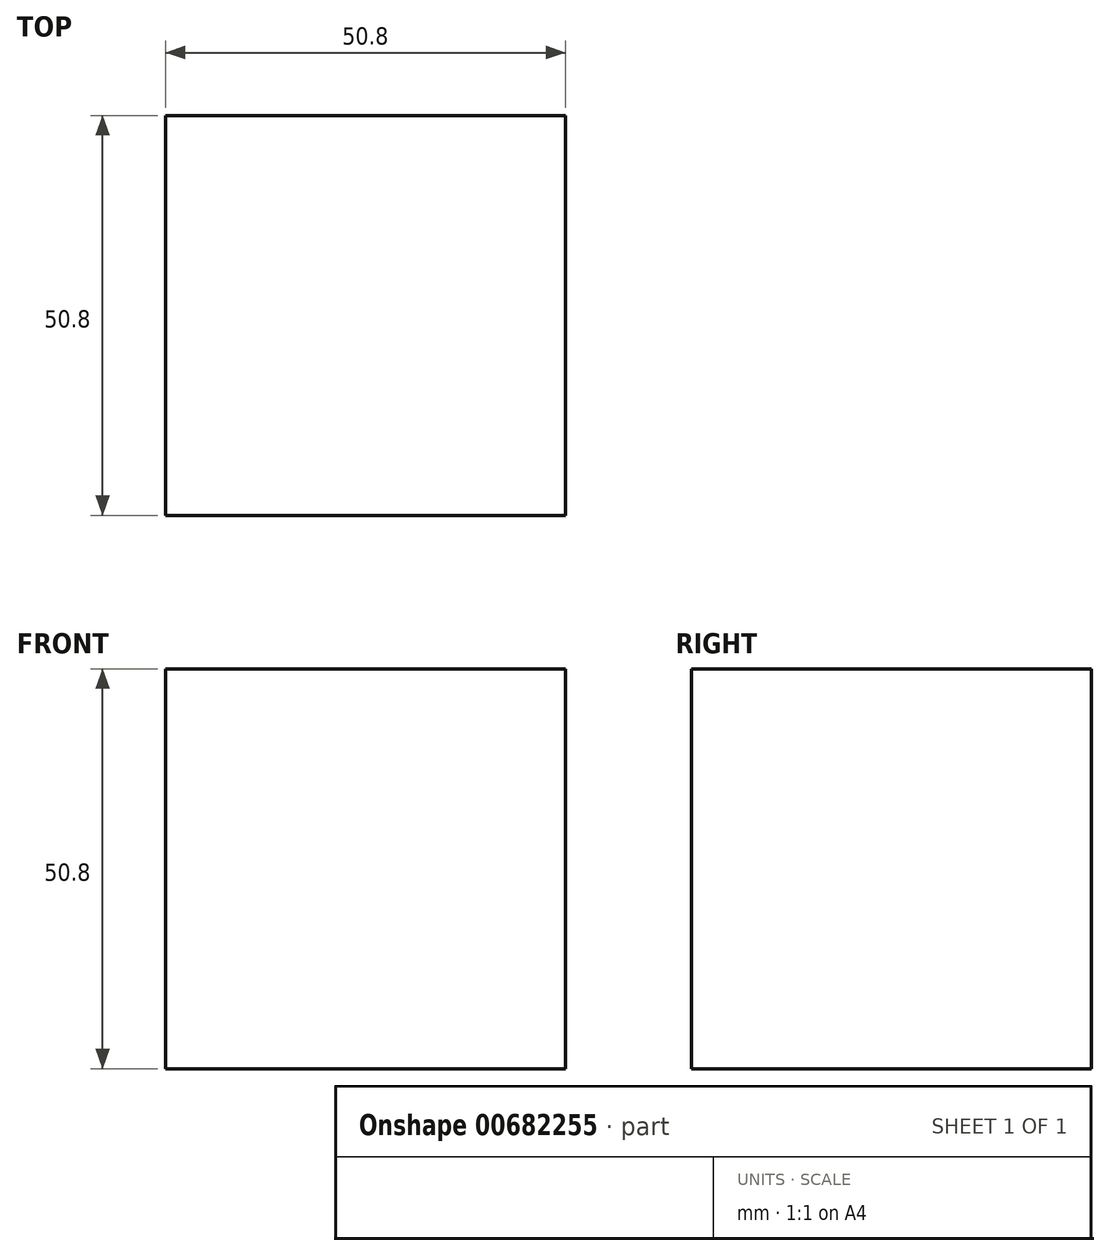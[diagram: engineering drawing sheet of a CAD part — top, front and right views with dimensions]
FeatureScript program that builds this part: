
annotation { "Feature Type Name" : "Feature", "Feature Type Description" : "" }
export const myFeature = defineFeature(function(context is Context, id is Id, definition is map)
    precondition{}
    {
        {
            var Q0;
            Q0=qCreatedBy(makeId("Front.planeOp"),FACE);
            var sketch = newSketch(context, id + "F0", { "sketchPlane" : qUnion([Q0])});
            skLineSegment(sketch, "E0", {"start": v(-44.7, 62.49) * mm, "end": v(-44.7, 11.69) * mm});
            skLineSegment(sketch, "E1", {"start": v(-44.7, 11.69) * mm, "end": v(6.1, 11.69) * mm});
            skLineSegment(sketch, "E2", {"start": v(6.1, 11.69) * mm, "end": v(6.1, 62.49) * mm});
            skLineSegment(sketch, "E3", {"start": v(6.1, 62.49) * mm, "end": v(-44.7, 62.49) * mm});
            skSolve(sketch);
        }
        {
            var Q0;
            Q0=makeQuery(id+"F0.imprint","IMPRINT",FACE,{"disambiguationData":[TD([[makeQuery(id+"F0.imprint","IMPRINT",EDGE,{"derivedFrom":sQuery(id+"F0.wireOp",EDGE,"E0")}),1.0]])]});
            extrude(context, id + "F1", {"entities" : qUnion([Q0]), "depth" : 50.8 * mm, "offsetDistance" : 25.4 * mm});
        }
    });
